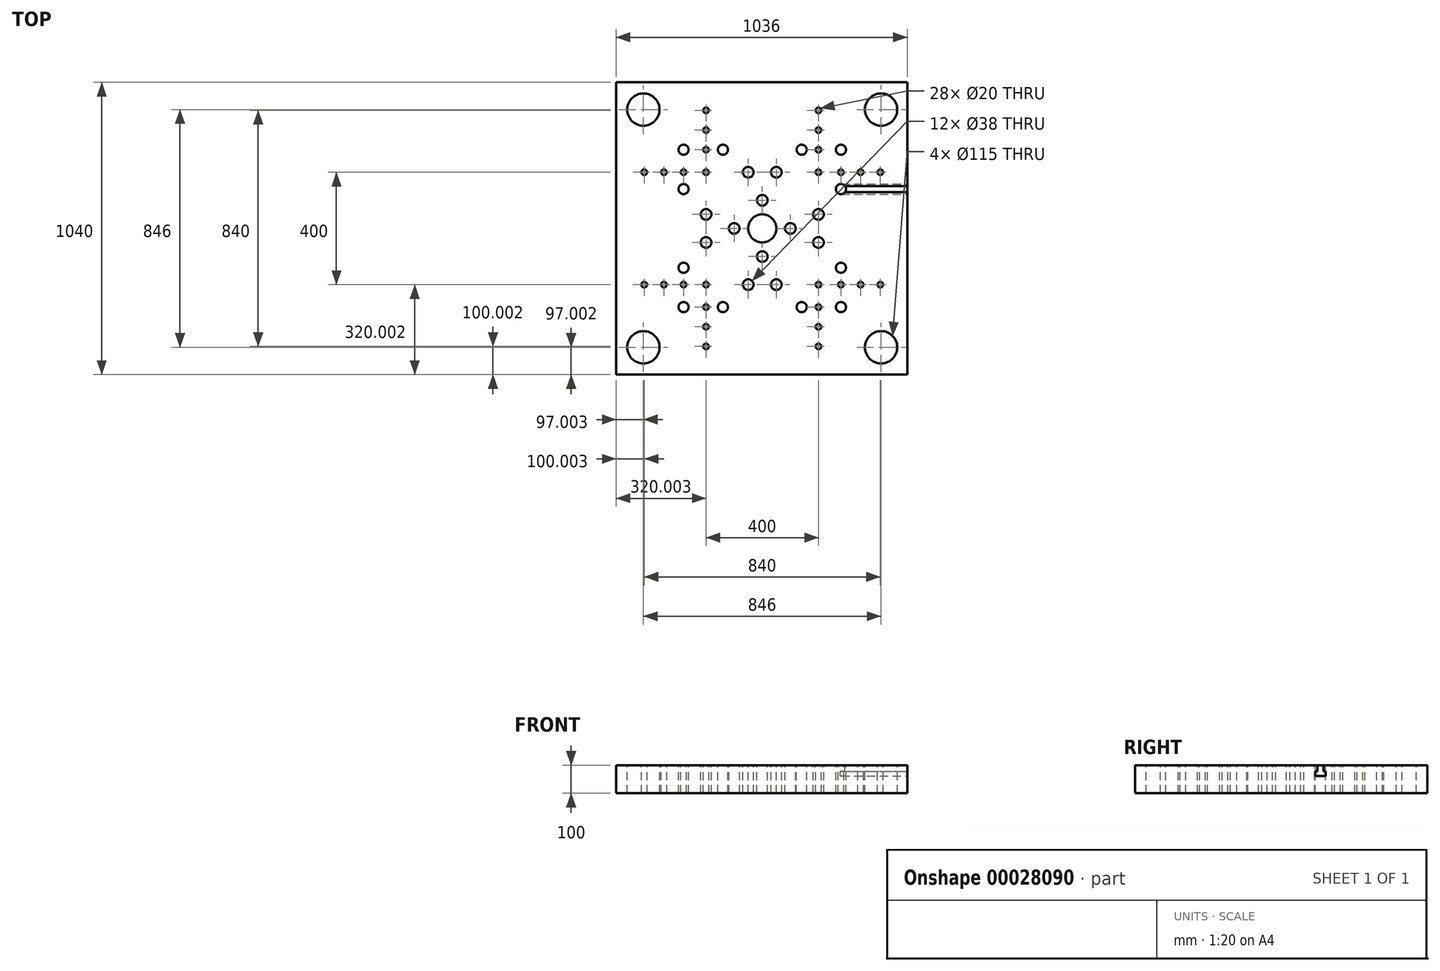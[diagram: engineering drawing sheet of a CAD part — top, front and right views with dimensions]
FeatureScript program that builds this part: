
annotation { "Feature Type Name" : "Feature", "Feature Type Description" : "" }
export const myFeature = defineFeature(function(context is Context, id is Id, definition is map)
    precondition{}
    {
        {
            var Q0;
            Q0=qCreatedBy(makeId("Top.planeOp"),FACE);
            var sketch = newSketch(context, id + "F0", { "sketchPlane" : qUnion([Q0])});
            skLineSegment(sketch, "E0.bottom", {"start": v(523.45, 499.73) * mm, "end": v(-512.55, 499.73) * mm});
            skLineSegment(sketch, "E0.top", {"start": v(523.45, -540.27) * mm, "end": v(-512.55, -540.27) * mm});
            skLineSegment(sketch, "E0.left", {"start": v(523.45, 499.73) * mm, "end": v(523.45, -540.27) * mm});
            skLineSegment(sketch, "E0.right", {"start": v(-512.55, 499.73) * mm, "end": v(-512.55, -540.27) * mm});
            skCircle(sketch, "E1", {"center": v(-415.55, 402.73) * mm, "radius": 57.5 * mm});
            skCircle(sketch, "E2.0.1.0", {"center": v(-415.55, -443.27) * mm, "radius": 57.5 * mm});
            skCircle(sketch, "E2.1.0.0", {"center": v(430.45, 402.73) * mm, "radius": 57.5 * mm});
            skCircle(sketch, "E2.1.1.0", {"center": v(430.45, -443.27) * mm, "radius": 57.5 * mm});
            skLineSegment(sketch, "E2.direction1", {"start": v(-415.55, 402.73) * mm, "end": v(430.45, 402.73) * mm, "construction": true});
            skLineSegment(sketch, "E2.direction2", {"start": v(-415.55, 402.73) * mm, "end": v(-415.55, -443.27) * mm, "construction": true});
            skCircle(sketch, "E3", {"center": v(7.45, -20.27) * mm, "radius": 50 * mm});
            skLineSegment(sketch, "E4", {"start": v(-989.57, -20.27) * mm, "end": v(1154.4, -20.27) * mm, "construction": true});
            skLineSegment(sketch, "E5", {"start": v(7.45, 822.56) * mm, "end": v(7.45, -802.5) * mm, "construction": true});
            skCircle(sketch, "E6", {"center": v(107.45, -20.27) * mm, "radius": 19 * mm});
            skCircle(sketch, "E7.1.0", {"center": v(7.45, -120.27) * mm, "radius": 19 * mm});
            skCircle(sketch, "E7.2.0", {"center": v(-92.55, -20.27) * mm, "radius": 19 * mm});
            skCircle(sketch, "E7.3.0", {"center": v(7.45, 79.73) * mm, "radius": 19 * mm});
            skLineSegment(sketch, "E7.anchor1", {"start": v(7.45, -20.27) * mm, "end": v(107.45, -20.27) * mm, "construction": true});
            skLineSegment(sketch, "E7.anchor2", {"start": v(7.45, -20.27) * mm, "end": v(7.45, 79.73) * mm, "construction": true});
            skCircle(sketch, "E8", {"center": v(207.45, -70.27) * mm, "radius": 19 * mm});
            skCircle(sketch, "E9.MirrorC", {"center": v(207.45, 29.73) * mm, "radius": 19 * mm});
            skCircle(sketch, "E10.1.0", {"center": v(57.45, -220.27) * mm, "radius": 19 * mm});
            skCircle(sketch, "E10.1.1", {"center": v(-42.55, -220.27) * mm, "radius": 19 * mm});
            skCircle(sketch, "E10.2.0", {"center": v(-192.55, -70.27) * mm, "radius": 19 * mm});
            skCircle(sketch, "E10.2.1", {"center": v(-192.55, 29.73) * mm, "radius": 19 * mm});
            skCircle(sketch, "E10.3.0", {"center": v(-42.55, 179.73) * mm, "radius": 19 * mm});
            skCircle(sketch, "E10.3.1", {"center": v(57.45, 179.73) * mm, "radius": 19 * mm});
            skLineSegment(sketch, "E10.anchor1", {"start": v(7.45, -20.27) * mm, "end": v(207.45, 29.73) * mm, "construction": true});
            skLineSegment(sketch, "E10.anchor2", {"start": v(7.45, -20.27) * mm, "end": v(-42.55, 179.73) * mm, "construction": true});
            skCircle(sketch, "E11", {"center": v(287.45, 259.73) * mm, "radius": 18 * mm});
            skCircle(sketch, "E12", {"center": v(147.45, 259.73) * mm, "radius": 18 * mm});
            skCircle(sketch, "E13", {"center": v(287.45, 119.73) * mm, "radius": 18 * mm});
            skCircle(sketch, "E14.1.0", {"center": v(147.45, -300.27) * mm, "radius": 18 * mm});
            skCircle(sketch, "E14.1.1", {"center": v(287.45, -300.27) * mm, "radius": 18 * mm});
            skCircle(sketch, "E14.1.2", {"center": v(287.45, -160.27) * mm, "radius": 18 * mm});
            skCircle(sketch, "E14.2.0", {"center": v(-272.55, -160.27) * mm, "radius": 18 * mm});
            skCircle(sketch, "E14.2.1", {"center": v(-272.55, -300.27) * mm, "radius": 18 * mm});
            skCircle(sketch, "E14.2.2", {"center": v(-132.55, -300.27) * mm, "radius": 18 * mm});
            skLineSegment(sketch, "E14.anchor1", {"start": v(7.45, -20.27) * mm, "end": v(287.45, 119.73) * mm, "construction": true});
            skLineSegment(sketch, "E14.anchor2", {"start": v(7.45, -20.27) * mm, "end": v(-132.55, 259.73) * mm, "construction": true});
            skCircle(sketch, "E15.1.3.0", {"center": v(-132.55, 259.73) * mm, "radius": 18 * mm});
            skCircle(sketch, "E15.2.3.0", {"center": v(-272.55, 259.73) * mm, "radius": 18 * mm});
            skCircle(sketch, "E15.4.3.0", {"center": v(-272.55, 119.73) * mm, "radius": 18 * mm});
            skCircle(sketch, "E16", {"center": v(-192.55, -440.27) * mm, "radius": 10 * mm});
            skCircle(sketch, "E17", {"center": v(-192.55, -370.27) * mm, "radius": 10 * mm});
            skCircle(sketch, "E18", {"center": v(-192.55, -300.27) * mm, "radius": 10 * mm});
            skCircle(sketch, "E19", {"center": v(-192.55, -220.27) * mm, "radius": 10 * mm});
            skCircle(sketch, "E20", {"center": v(-272.55, -220.27) * mm, "radius": 10 * mm});
            skCircle(sketch, "E21", {"center": v(-342.55, -220.27) * mm, "radius": 10 * mm});
            skCircle(sketch, "E22", {"center": v(-412.55, -220.27) * mm, "radius": 10 * mm});
            skCircle(sketch, "E23.1.0", {"center": v(-192.55, 399.73) * mm, "radius": 10 * mm});
            skCircle(sketch, "E23.1.1", {"center": v(-192.55, 329.73) * mm, "radius": 10 * mm});
            skCircle(sketch, "E23.1.2", {"center": v(-192.55, 259.73) * mm, "radius": 10 * mm});
            skCircle(sketch, "E23.1.3", {"center": v(-192.55, 179.73) * mm, "radius": 10 * mm});
            skCircle(sketch, "E23.1.4", {"center": v(-272.55, 179.73) * mm, "radius": 10 * mm});
            skCircle(sketch, "E23.1.5", {"center": v(-342.55, 179.73) * mm, "radius": 10 * mm});
            skCircle(sketch, "E23.1.6", {"center": v(-412.55, 179.73) * mm, "radius": 10 * mm});
            skCircle(sketch, "E23.2.0", {"center": v(427.45, 179.73) * mm, "radius": 10 * mm});
            skCircle(sketch, "E23.2.1", {"center": v(357.45, 179.73) * mm, "radius": 10 * mm});
            skCircle(sketch, "E23.2.2", {"center": v(287.45, 179.73) * mm, "radius": 10 * mm});
            skCircle(sketch, "E23.2.3", {"center": v(207.45, 179.73) * mm, "radius": 10 * mm});
            skCircle(sketch, "E23.2.4", {"center": v(207.45, 259.73) * mm, "radius": 10 * mm});
            skCircle(sketch, "E23.2.5", {"center": v(207.45, 329.73) * mm, "radius": 10 * mm});
            skCircle(sketch, "E23.2.6", {"center": v(207.45, 399.73) * mm, "radius": 10 * mm});
            skCircle(sketch, "E23.3.0", {"center": v(207.45, -440.27) * mm, "radius": 10 * mm});
            skCircle(sketch, "E23.3.1", {"center": v(207.45, -370.27) * mm, "radius": 10 * mm});
            skCircle(sketch, "E23.3.2", {"center": v(207.45, -300.27) * mm, "radius": 10 * mm});
            skCircle(sketch, "E23.3.3", {"center": v(207.45, -220.27) * mm, "radius": 10 * mm});
            skCircle(sketch, "E23.3.4", {"center": v(287.45, -220.27) * mm, "radius": 10 * mm});
            skCircle(sketch, "E23.3.5", {"center": v(357.45, -220.27) * mm, "radius": 10 * mm});
            skCircle(sketch, "E23.3.6", {"center": v(427.45, -220.27) * mm, "radius": 10 * mm});
            skLineSegment(sketch, "E23.anchor1", {"start": v(7.45, -20.27) * mm, "end": v(-412.55, -220.27) * mm, "construction": true});
            skLineSegment(sketch, "E23.anchor2", {"start": v(7.45, -20.27) * mm, "end": v(207.45, -440.27) * mm, "construction": true});
            skSolve(sketch);
        }
        {
            var Q0;
            Q0 = qSketchRegion(id + "F0", true);
            extrude(context, id + "F1", {"entities" : qUnion([Q0]), "oppositeDirection" : true, "depth" : 100 * mm});
        }
        {
            var Q0;
            Q0=makeQuery(id+"F1.opExtrude","SWEPT_FACE",FACE,{"disambiguationData":[OSD([sQuery(id+"F0.wireOp",EDGE,"E0.left")])]});
            var sketch = newSketch(context, id + "F2", { "sketchPlane" : qUnion([Q0])});
            skLineSegment(sketch, "E24", {"start": v(-20.27, 0) * mm, "end": v(-20.27, -191.05) * mm, "construction": true});
            skLineSegment(sketch, "E25", {"start": v(119.73, 34.63) * mm, "end": v(119.73, -200.7) * mm, "construction": true});
            skLineSegment(sketch, "E26", {"start": v(108.73, 16.81) * mm, "end": v(108.73, -22) * mm});
            skLineSegment(sketch, "E27.MirrorCS", {"start": v(130.73, 16.81) * mm, "end": v(130.73, -22) * mm});
            skLineSegment(sketch, "E28", {"start": v(101.73, -22) * mm, "end": v(108.73, -22) * mm});
            skLineSegment(sketch, "E29", {"start": v(101.73, -38) * mm, "end": v(137.73, -38) * mm});
            skLineSegment(sketch, "E30", {"start": v(101.73, -22) * mm, "end": v(101.73, -38) * mm});
            skLineSegment(sketch, "E31.MirrorCS", {"start": v(137.73, -22) * mm, "end": v(137.73, -38) * mm});
            skLineSegment(sketch, "E32", {"start": v(108.73, 16.81) * mm, "end": v(130.73, 16.81) * mm});
            skPoint(sketch, "E33.orphan", {"position": v(101.73, -11.4) * mm});
            skPoint(sketch, "E34.orphan", {"position": v(101.73, -57.42) * mm});
            skPoint(sketch, "E35.orphan", {"position": v(108.73, -50) * mm});
            skLineSegment(sketch, "E36.trimOffspring", {"start": v(130.73, -22) * mm, "end": v(137.73, -22) * mm});
            skPoint(sketch, "E37.orphan", {"position": v(137.73, -11.4) * mm});
            skPoint(sketch, "E38.orphan", {"position": v(137.73, -57.42) * mm});
            skPoint(sketch, "E39.trimOffspring.end.orphan", {"position": v(130.73, -50) * mm});
            skSolve(sketch);
        }
        {
            var Q0;
            Q0 = qSketchRegion(id + "F2", true);
            extrude(context, id + "F3", {"entities" : qUnion([Q0]), "operationType" : NewBodyOperationType.REMOVE, "oppositeDirection" : true, "depth" : ((1036 - 560) / 2) * mm});
        }
    });
